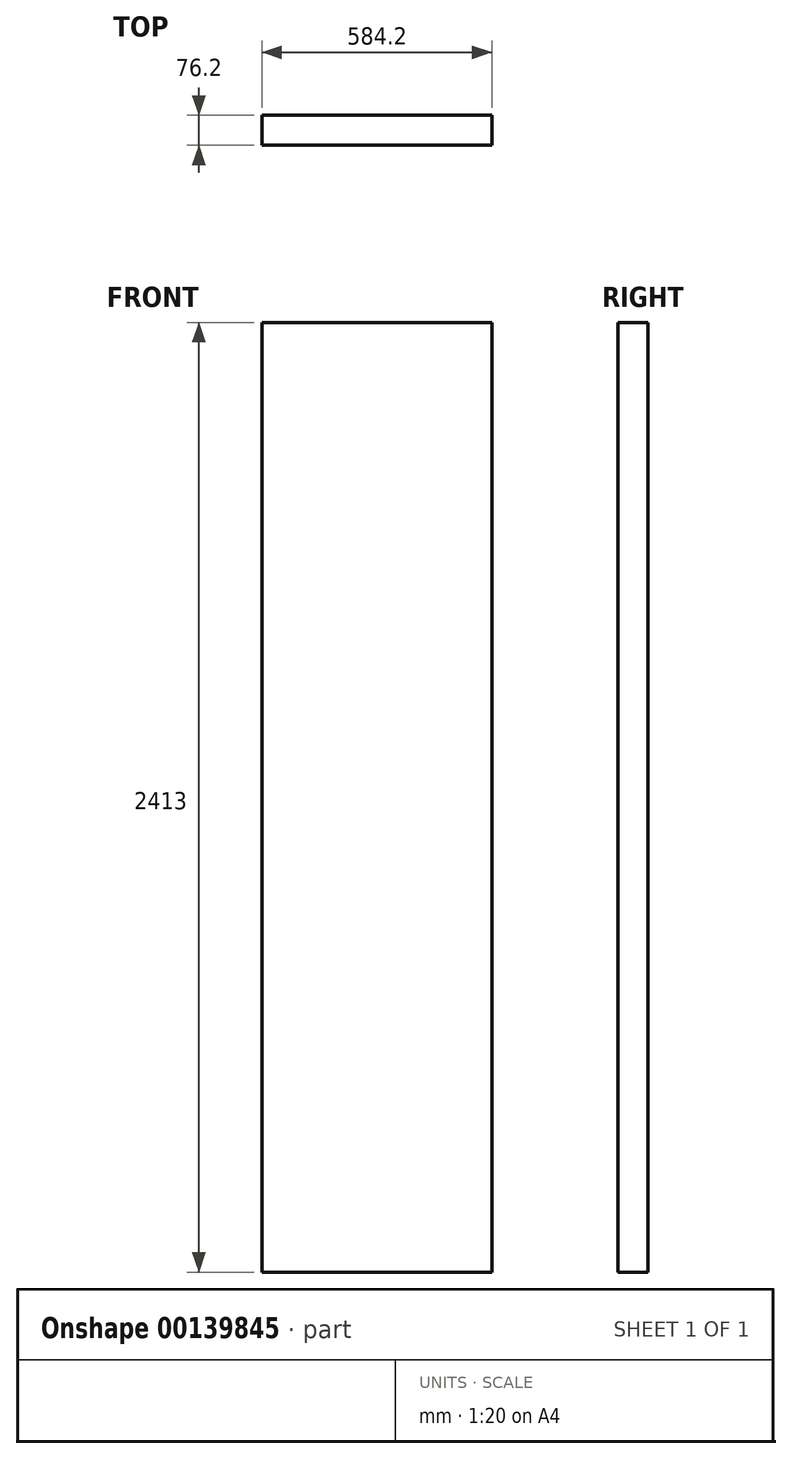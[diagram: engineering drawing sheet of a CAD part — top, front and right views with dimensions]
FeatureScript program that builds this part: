
annotation { "Feature Type Name" : "Feature", "Feature Type Description" : "" }
export const myFeature = defineFeature(function(context is Context, id is Id, definition is map)
    precondition{}
    {
        {
            var Q0;
            Q0=qCreatedBy(makeId("Front.planeOp"),FACE);
            var sketch = newSketch(context, id + "F0", { "sketchPlane" : qUnion([Q0])});
            skLineSegment(sketch, "E0.bottom", {"start": v(292.1, 1206.5) * mm, "end": v(-292.1, 1206.5) * mm});
            skLineSegment(sketch, "E0.top", {"start": v(292.1, -1206.5) * mm, "end": v(-292.1, -1206.5) * mm});
            skLineSegment(sketch, "E0.left", {"start": v(292.1, 1206.5) * mm, "end": v(292.1, -1206.5) * mm});
            skLineSegment(sketch, "E0.right", {"start": v(-292.1, 1206.5) * mm, "end": v(-292.1, -1206.5) * mm});
            skPoint(sketch, "E0.middle", {"position": v(0, 0) * mm});
            skSolve(sketch);
        }
        {
            var Q0;
            Q0 = qSketchRegion(id + "F0", true);
            extrude(context, id + "F1", {"entities" : qUnion([Q0]), "depth" : 76.2 * mm});
        }
    });
